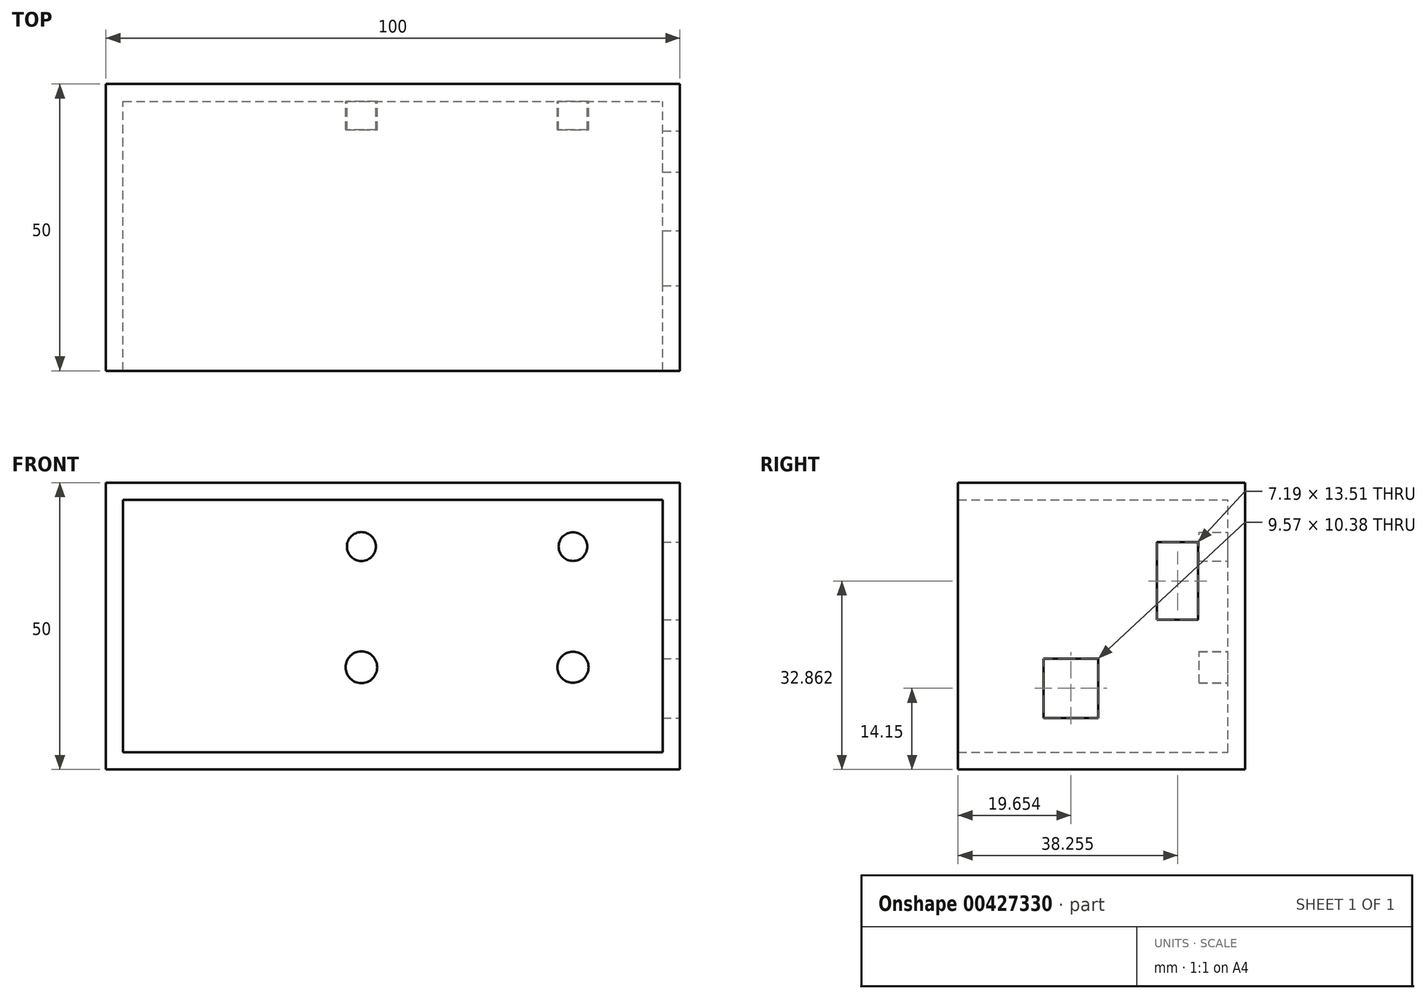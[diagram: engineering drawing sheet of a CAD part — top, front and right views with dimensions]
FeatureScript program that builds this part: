
annotation { "Feature Type Name" : "Feature", "Feature Type Description" : "" }
export const myFeature = defineFeature(function(context is Context, id is Id, definition is map)
    precondition{}
    {
        {
            var Q0;
            Q0=qCreatedBy(makeId("Front.planeOp"),FACE);
            var sketch = newSketch(context, id + "F0", { "sketchPlane" : qUnion([Q0])});
            skLineSegment(sketch, "E0.bottom", {"start": v(-59.89, -35.98) * mm, "end": v(40.11, -35.98) * mm});
            skLineSegment(sketch, "E0.top", {"start": v(-59.89, 14.02) * mm, "end": v(40.11, 14.02) * mm});
            skLineSegment(sketch, "E0.left", {"start": v(-59.89, -35.98) * mm, "end": v(-59.89, 14.02) * mm});
            skLineSegment(sketch, "E0.right", {"start": v(40.11, -35.98) * mm, "end": v(40.11, 14.02) * mm});
            skSolve(sketch);
        }
        {
            var Q0;
            Q0 = qSketchRegion(id + "F0", true);
            extrude(context, id + "F1", {"entities" : qUnion([Q0]), "depth" : 50 * mm});
        }
        {
            var Q0;
            Q0=makeQuery(id+"F1.opExtrude","CAP_FACE",FACE,{"disambiguationData":[OSD([sQuery(id+"F0.wireOp",EDGE,"E0.bottom"),sQuery(id+"F0.wireOp",EDGE,"E0.top"),sQuery(id+"F0.wireOp",EDGE,"E0.left"),sQuery(id+"F0.wireOp",EDGE,"E0.right")])],"isStart":false});
            shell(context, id + "F2", {"entities" : qUnion([Q0]), "thickness" : 3 * mm});
        }
        {
            var Q0;
            Q0=makeQuery(id+"F1.opExtrude","SWEPT_FACE",FACE,{"disambiguationData":[OSD([sQuery(id+"F0.wireOp",EDGE,"E0.right")])]});
            var sketch = newSketch(context, id + "F3", { "sketchPlane" : qUnion([Q0])});
            skLineSegment(sketch, "E1.bottom", {"start": v(-15.34, 3.64) * mm, "end": v(-8.15, 3.64) * mm});
            skLineSegment(sketch, "E1.top", {"start": v(-15.34, -9.87) * mm, "end": v(-8.15, -9.87) * mm});
            skLineSegment(sketch, "E1.left", {"start": v(-15.34, 3.64) * mm, "end": v(-15.34, -9.87) * mm});
            skLineSegment(sketch, "E1.right", {"start": v(-8.15, 3.64) * mm, "end": v(-8.15, -9.87) * mm});
            skLineSegment(sketch, "E2.bottom", {"start": v(-35.13, -16.64) * mm, "end": v(-25.56, -16.64) * mm});
            skLineSegment(sketch, "E2.top", {"start": v(-35.13, -27.02) * mm, "end": v(-25.56, -27.02) * mm});
            skLineSegment(sketch, "E2.left", {"start": v(-35.13, -16.64) * mm, "end": v(-35.13, -27.02) * mm});
            skLineSegment(sketch, "E2.right", {"start": v(-25.56, -16.64) * mm, "end": v(-25.56, -27.02) * mm});
            skSolve(sketch);
        }
        {
            var Q0;
            Q0=makeQuery(id+"F3.imprint","IMPRINT",FACE,{"disambiguationData":[TD([[makeQuery(id+"F3.imprint","IMPRINT",EDGE,{"derivedFrom":sQuery(id+"F3.wireOp",EDGE,"E1.bottom")}),-1.0]])]});
            extrude(context, id + "F4", {"entities" : qUnion([Q0]), "operationType" : NewBodyOperationType.REMOVE, "oppositeDirection" : true, "depth" : 3 * mm});
        }
        {
            var Q0;
            Q0=makeQuery(id+"F3.imprint","IMPRINT",FACE,{"disambiguationData":[TD([[makeQuery(id+"F3.imprint","IMPRINT",EDGE,{"derivedFrom":sQuery(id+"F3.wireOp",EDGE,"E2.bottom")}),-1.0]])]});
            extrude(context, id + "F5", {"entities" : qUnion([Q0]), "operationType" : NewBodyOperationType.REMOVE, "oppositeDirection" : true, "depth" : 3 * mm});
        }
        {
            var Q0;
            Q0=makeQuery(id+"F2.opShell","OFFSET_FACE",FACE,{"disambiguationData":[OSD([sQuery(id+"F0.wireOp",EDGE,"E0.bottom"),sQuery(id+"F0.wireOp",EDGE,"E0.top"),sQuery(id+"F0.wireOp",EDGE,"E0.left"),sQuery(id+"F0.wireOp",EDGE,"E0.right")])]});
            var sketch = newSketch(context, id + "F6", { "sketchPlane" : qUnion([Q0])});
            skCircle(sketch, "E3", {"center": v(21.5, 2.88) * mm, "radius": 2.5 * mm});
            skCircle(sketch, "E4", {"center": v(21.5, -18.16) * mm, "radius": 2.72 * mm});
            skCircle(sketch, "E5", {"center": v(-15.37, 2.88) * mm, "radius": 2.52 * mm});
            skCircle(sketch, "E6", {"center": v(-15.37, -18.16) * mm, "radius": 2.76 * mm});
            skSolve(sketch);
        }
        {
            var Q0;
            Q0=makeQuery(id+"F6.imprint","IMPRINT",FACE,{"disambiguationData":[TD([[makeQuery(id+"F6.imprint","IMPRINT",EDGE,{"derivedFrom":sQuery(id+"F6.wireOp",EDGE,"E3")}),1.0]])]});
            var Q1;
            Q1=sQuery(id+"F6.wireOp",EDGE,"E3");
            extrude(context, id + "F7", {"entities" : qUnion([Q0]), "operationType" : NewBodyOperationType.ADD, "surfaceEntities" : qUnion([Q1]), "depth" : 5 * mm});
        }
        {
            var Q0;
            Q0=makeQuery(id+"F6.imprint","IMPRINT",FACE,{"disambiguationData":[TD([[makeQuery(id+"F6.imprint","IMPRINT",EDGE,{"derivedFrom":sQuery(id+"F6.wireOp",EDGE,"E4")}),1.0]])]});
            var Q1;
            Q1=sQuery(id+"F6.wireOp",EDGE,"E4");
            extrude(context, id + "F8", {"entities" : qUnion([Q0]), "operationType" : NewBodyOperationType.ADD, "surfaceEntities" : qUnion([Q1]), "depth" : 5 * mm});
        }
        {
            var Q0;
            Q0=makeQuery(id+"F6.imprint","IMPRINT",FACE,{"disambiguationData":[TD([[makeQuery(id+"F6.imprint","IMPRINT",EDGE,{"derivedFrom":sQuery(id+"F6.wireOp",EDGE,"E6")}),1.0]])]});
            extrude(context, id + "F9", {"entities" : qUnion([Q0]), "operationType" : NewBodyOperationType.ADD, "depth" : 5 * mm});
        }
        {
            var Q0;
            Q0=makeQuery(id+"F6.imprint","IMPRINT",FACE,{"disambiguationData":[TD([[makeQuery(id+"F6.imprint","IMPRINT",EDGE,{"derivedFrom":sQuery(id+"F6.wireOp",EDGE,"E5")}),1.0]])]});
            extrude(context, id + "F10", {"entities" : qUnion([Q0]), "operationType" : NewBodyOperationType.ADD, "depth" : 5 * mm});
        }
    });
